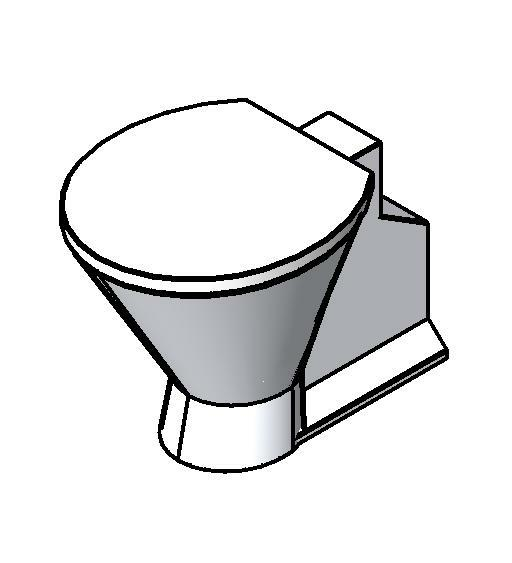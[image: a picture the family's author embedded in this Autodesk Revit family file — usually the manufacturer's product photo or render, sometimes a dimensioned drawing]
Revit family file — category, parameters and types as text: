
# Revit family: Deca_Bica para lavatório mesa wave média_Deca You_1791.106
name_source: partatom
category: Plumbing Fixtures
units: mm (PartAtom-declared; Revit-internal decimal feet)

## family parameters
Cut with Voids When Loaded = No
Host = Face
Part Type = Normal
Room Calculation Point = No
Round Connector Dimension = Use Radius
Shared = No

## types (10) — shared parameters
Acompanha o Produto = Restritor de Vazão Deca Comfort
Aprovado por = quattroD
Atendimento ao Cliente = 0800-0117073
Categoria = Bica Lavatório / Banheiro
Composição Básica = Liga de Cobre (Latão),Plásticos de Engenharia e Elastômeros
Consumo = -
Cor Secundária = -
Criado por = quattroD
Itens de Instalação = Mangeira Flexivel
Linha = Deca You
Manufacturer = DECA
Norma = Não possui
Pressão mín. Aquec. Acúmulo = -
Pressão mín. Aquec. Passagem = -
Saída de Esgoto = -
Segmento = Luxo
Tipo de dispositivo economizador = Decacomfort
Tipo de mecanismo utilizado = Não Possui
Tipo de rosca de entrada = BSP
Tipo de rosca de saída = -
URL = www.deca.com.br
zero-valued in all types: CWFU, Default Elevation, Diâmetro Ponto de Esgoto, Diâmetro Água Fria, Peso Líquido (Kg), Raio Ponto de Esgoto, Raio Água Fria, WFU

## per-type parameters (varying)
| type | Cor Principal | Código Pai | Material | Model |
| 1791.BL106.MT_Black Matte | Black Matte | 1791.BL106.MT | Deca_Black Matte | 1791.BL106.MT |
| 1791.GF106.MT_Antracite | Antracite Dark | 1791.GF106.MT | Deca_Antracite | 1791.GF106.MT |
| 1791.INX106_Inox | Inox | 1791.INX106 | Deca_Inox | 1791.INX106 |
| 1791.SM106.MT_Summer Gold | SUMMER GOLD | 1791.SM106.MT | Deca_Summer Gold | 1791.SM106.MT |
| 1791.MR106.MT_Brown Matte | Dynamic Brown | 1791.MR106.MT | Deca_Brown Matte | 1791.MR106.MT |
| 1791.LS106.MT_Dynamic Gold | Dynamic Gold | 1791.LS106.MT | Deca_Dynamic Gold | 1791.LS106.MT |
| 1791.CL106.MT_Dynamic Peach | Dynamic Brown | 1791.CL106.MT | Deca_Dynamic Peach | 1791.CL106.MT |
| 1791.AZ106.MT_Dynamic Blue | Dynamic Blue | 1791.AZ106.MT | Dynamic Blue | 1791.AZ106.MT |
| 1791.BR106.MT_Dynamic White | Dynamic White | 1791.BR106.MT | Dynamic White | 1791.BR106.MT |
| 1791.LV106.MT_Dynamic Lilac | Dynamic Lilac | 1791.LV106.MT | Dynamic Lilac | 1791.LV106.MT |

## geometry (parser evidence)
native form markers: Sweep x1
no freeform markers — native parametric forms only
